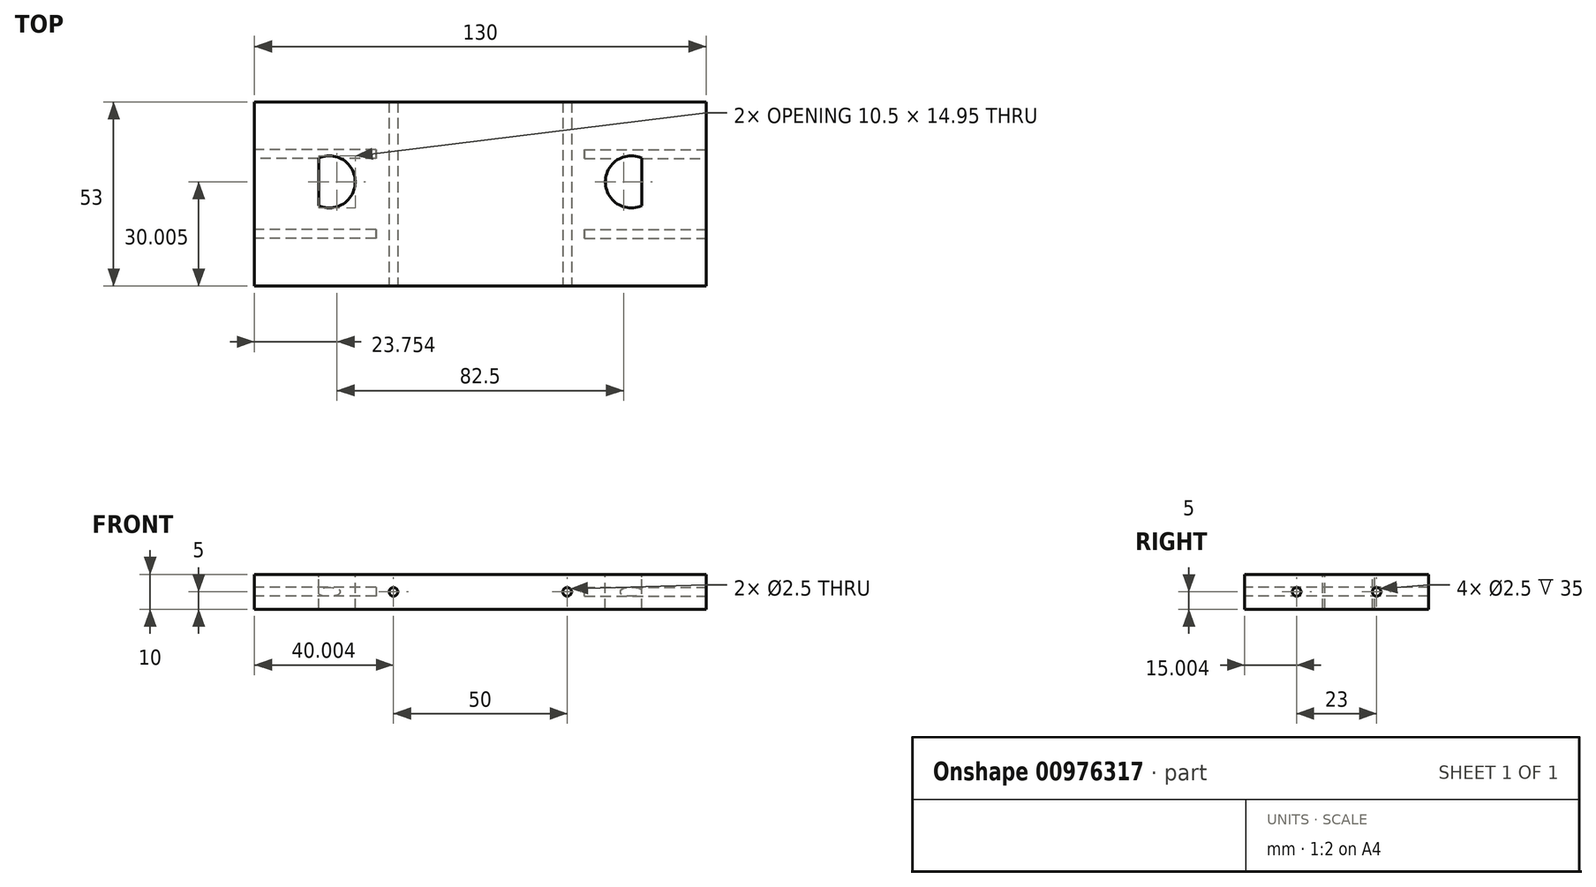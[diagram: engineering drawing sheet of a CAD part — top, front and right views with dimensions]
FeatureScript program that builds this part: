
annotation { "Feature Type Name" : "Feature", "Feature Type Description" : "" }
export const myFeature = defineFeature(function(context is Context, id is Id, definition is map)
    precondition{}
    {
        {
            var Q0;
            Q0=qCreatedBy(makeId("Top.planeOp"),FACE);
            var sketch = newSketch(context, id + "F0", { "sketchPlane" : qUnion([Q0])});
            skLineSegment(sketch, "E0.bottom", {"start": v(-44.98, 28.62) * mm, "end": v(85.02, 28.62) * mm});
            skLineSegment(sketch, "E0.top", {"start": v(-44.98, -24.38) * mm, "end": v(85.02, -24.38) * mm});
            skLineSegment(sketch, "E0.left", {"start": v(-44.98, 28.62) * mm, "end": v(-44.98, -24.38) * mm});
            skLineSegment(sketch, "E0.right", {"start": v(85.02, 28.62) * mm, "end": v(85.02, -24.38) * mm});
            skSolve(sketch);
        }
        {
            var Q0;
            Q0=makeQuery(id+"F0.imprint","IMPRINT",FACE,{"disambiguationData":[TD([[makeQuery(id+"F0.imprint","IMPRINT",EDGE,{"derivedFrom":sQuery(id+"F0.wireOp",EDGE,"E0.bottom")}),-1.0]])]});
            extrude(context, id + "F1", {"entities" : qUnion([Q0]), "depth" : 10 * mm, "offsetDistance" : 25 * mm});
        }
        {
            var Q0;
            Q0=makeQuery(id+"F1.opExtrude","SWEPT_FACE",FACE,{"disambiguationData":[OSD([sQuery(id+"F0.wireOp",EDGE,"E0.right")])]});
            var sketch = newSketch(context, id + "F2", { "sketchPlane" : qUnion([Q0])});
            skCircle(sketch, "E1", {"center": v(-9.38, 5) * mm, "radius": 1.25 * mm});
            skCircle(sketch, "E2", {"center": v(13.62, 5) * mm, "radius": 1.25 * mm});
            skSolve(sketch);
        }
        {
            var Q0;
            Q0=makeQuery(id+"F1.opExtrude","SWEPT_FACE",FACE,{"disambiguationData":[OSD([sQuery(id+"F0.wireOp",EDGE,"E0.top")])]});
            var sketch = newSketch(context, id + "F3", { "sketchPlane" : qUnion([Q0])});
            skCircle(sketch, "E3", {"center": v(-4.98, 5) * mm, "radius": 1.25 * mm});
            skCircle(sketch, "E4", {"center": v(45.02, 5) * mm, "radius": 1.25 * mm});
            skSolve(sketch);
        }
        {
            var Q0;
            Q0=makeQuery(id+"F1.opExtrude","SWEPT_FACE",FACE,{"disambiguationData":[OSD([sQuery(id+"F0.wireOp",EDGE,"E0.left")])]});
            var sketch = newSketch(context, id + "F4", { "sketchPlane" : qUnion([Q0])});
            skCircle(sketch, "E5", {"center": v(-13.62, 5) * mm, "radius": 1.25 * mm});
            skCircle(sketch, "E6", {"center": v(9.38, 5) * mm, "radius": 1.25 * mm});
            skSolve(sketch);
        }
        {
            var Q0;
            Q0 = qSketchRegion(id + "F2", true);
            extrude(context, id + "F5", {"entities" : qUnion([Q0]), "operationType" : NewBodyOperationType.REMOVE, "oppositeDirection" : true, "depth" : 35 * mm, "offsetDistance" : 25 * mm});
        }
        {
            var Q0;
            Q0 = qSketchRegion(id + "F3", true);
            extrude(context, id + "F6", {"entities" : qUnion([Q0]), "operationType" : NewBodyOperationType.REMOVE, "endBound" : BoundingType.UP_TO_NEXT, "oppositeDirection" : true, "depth" : 25 * mm, "offsetDistance" : 25 * mm});
        }
        {
            var Q0;
            Q0 = qSketchRegion(id + "F4", true);
            extrude(context, id + "F7", {"entities" : qUnion([Q0]), "operationType" : NewBodyOperationType.REMOVE, "oppositeDirection" : true, "depth" : 35 * mm, "offsetDistance" : 25 * mm});
        }
        {
            var Q0;
            Q0=makeQuery(id+"F1.opExtrude","CAP_FACE",FACE,{"disambiguationData":[OSD([sQuery(id+"F0.wireOp",EDGE,"E0.bottom"),sQuery(id+"F0.wireOp",EDGE,"E0.top"),sQuery(id+"F0.wireOp",EDGE,"E0.left"),sQuery(id+"F0.wireOp",EDGE,"E0.right")])],"isStart":false});
            var sketch = newSketch(context, id + "F8", { "sketchPlane" : qUnion([Q0])});
            skCircle(sketch, "E7", {"center": v(-23.48, 5.62) * mm, "radius": 7.5 * mm});
            skCircle(sketch, "E8", {"center": v(63.52, 5.62) * mm, "radius": 7.5 * mm});
            skLineSegment(sketch, "E9", {"start": v(-26.48, 12.5) * mm, "end": v(-26.48, -1.25) * mm});
            skLineSegment(sketch, "E10", {"start": v(66.52, 12.5) * mm, "end": v(66.52, -1.25) * mm});
            skSolve(sketch);
        }
        {
            var Q0;
            {var subQ0=sQuery(id+"F8.wireOp",EDGE,"E10");Q0=makeQuery(id+"F8.imprint","IMPRINT",FACE,{"disambiguationData":[TD([[makeQuery(id+"F8.imprint","IMPRINT",EDGE,{"derivedFrom":subQ0}),-1.0]])]});}
            var Q1;
            {var subQ0=sQuery(id+"F8.wireOp",EDGE,"E9");Q1=makeQuery(id+"F8.imprint","IMPRINT",FACE,{"disambiguationData":[TD([[makeQuery(id+"F8.imprint","IMPRINT",EDGE,{"derivedFrom":subQ0}),1.0]])]});}
            extrude(context, id + "F9", {"entities" : qUnion([Q0, Q1]), "operationType" : NewBodyOperationType.REMOVE, "endBound" : BoundingType.UP_TO_NEXT, "oppositeDirection" : true, "depth" : 25 * mm, "offsetDistance" : 25 * mm});
        }
    });
